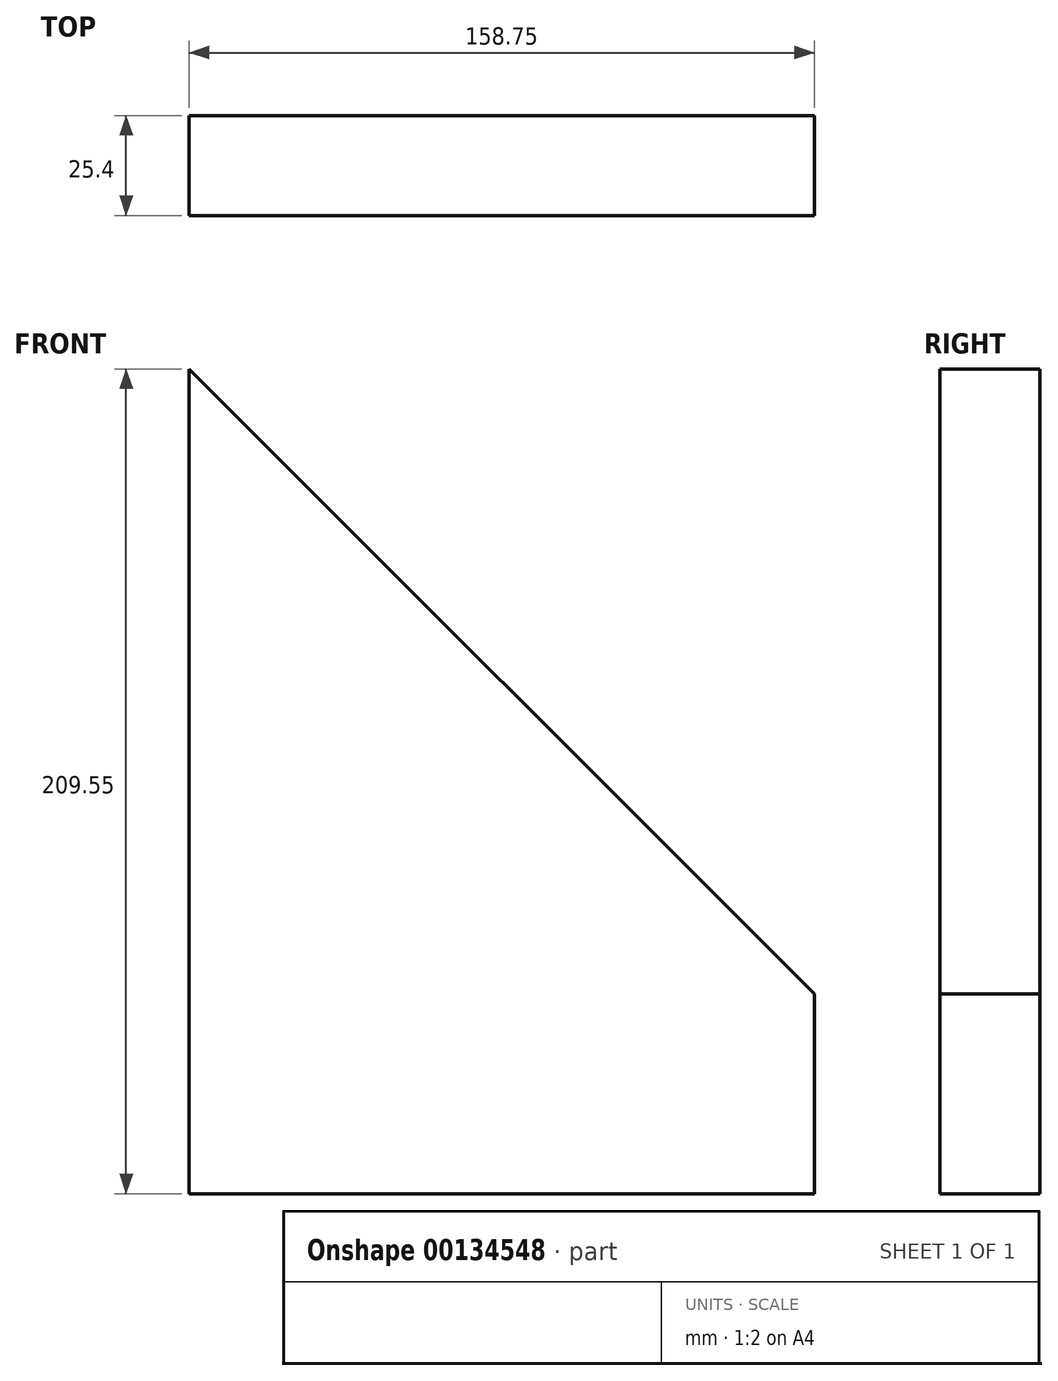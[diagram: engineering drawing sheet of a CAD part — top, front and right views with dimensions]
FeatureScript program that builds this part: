
annotation { "Feature Type Name" : "Feature", "Feature Type Description" : "" }
export const myFeature = defineFeature(function(context is Context, id is Id, definition is map)
    precondition{}
    {
        {
            var Q0;
            Q0=qCreatedBy(makeId("Front.planeOp"),FACE);
            var sketch = newSketch(context, id + "F0", { "sketchPlane" : qUnion([Q0])});
            skLineSegment(sketch, "E0", {"start": v(-31.3, 194.53) * mm, "end": v(-31.3, -15.02) * mm});
            skLineSegment(sketch, "E1", {"start": v(-31.3, -15.02) * mm, "end": v(127.45, -15.02) * mm});
            skLineSegment(sketch, "E2", {"start": v(127.45, -15.02) * mm, "end": v(127.45, 35.78) * mm});
            skLineSegment(sketch, "E3", {"start": v(127.45, 35.78) * mm, "end": v(-31.3, 194.53) * mm});
            skSolve(sketch);
        }
        {
            var Q0;
            Q0=makeQuery(id+"F0.imprint","IMPRINT",FACE,{"disambiguationData":[TD([[makeQuery(id+"F0.imprint","IMPRINT",EDGE,{"derivedFrom":sQuery(id+"F0.wireOp",EDGE,"E0")}),1.0]])]});
            extrude(context, id + "F1", {"entities" : qUnion([Q0]), "depth" : 25.4 * mm});
        }
    });
